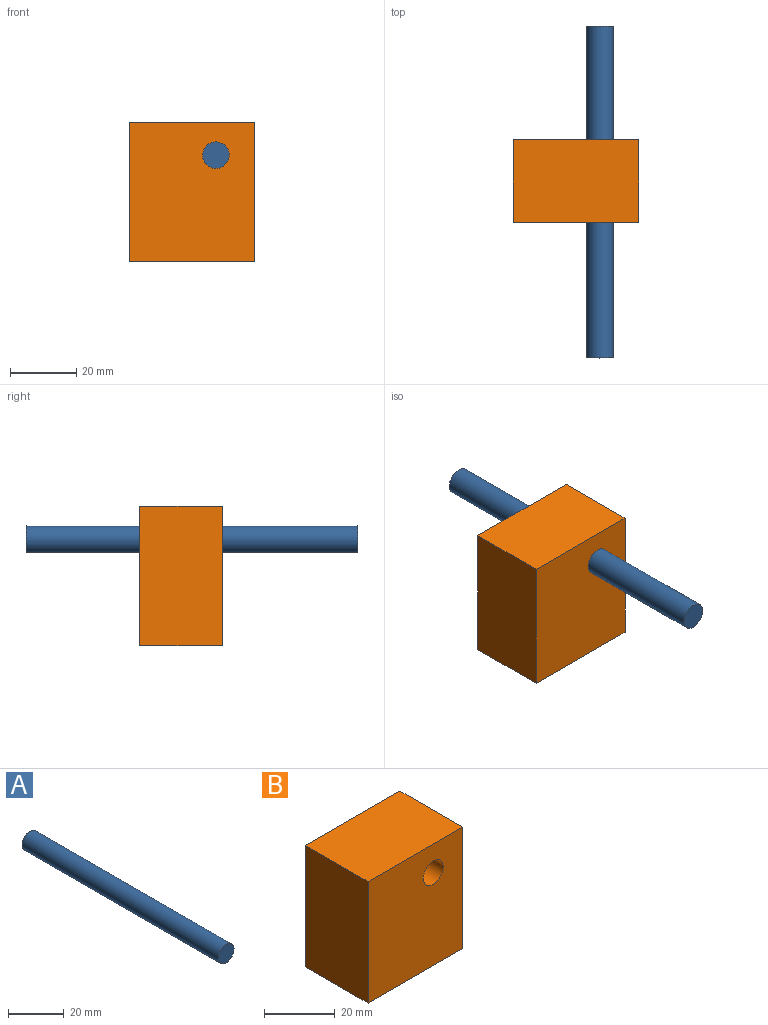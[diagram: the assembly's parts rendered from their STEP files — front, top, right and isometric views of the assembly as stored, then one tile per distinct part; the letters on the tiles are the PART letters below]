
ASSEMBLY  parts=2 mates=1
PART A: 3 faces, bbox 8x100x8 mm
  f0: cylinder r=4mm len=100mm, axis (0,1,0), area 2513.3mm2, adj f1,f2
  f1: plane 8x8mm, normal (0,-1,0), area 50.3mm2, adj f0
  f2: plane 8x8mm, normal (0,1,0), area 50.3mm2, adj f0
PART B: 7 faces, bbox 37.8x25x42.1 mm
  f0: plane 37.77x25mm, normal (0,0,1), area 944.2mm2, adj f1,f3,f4,f5
  f1: plane 42.05x25mm, normal (-1,0,0), area 1051.3mm2, adj f0,f2,f4,f5
  f2: plane 37.77x25mm, normal (0,0,-1), area 944.2mm2, adj f1,f3,f4,f5
  f3: plane 42.05x25mm, normal (1,0,0), area 1051.3mm2, adj f0,f2,f4,f5
  f4: plane 42.05x37.77mm, normal (0,-1,0), area 1538mm2, adj f0,f1,f2,f3,f6
  f5: plane 42.05x37.77mm, normal (0,1,0), area 1538mm2, adj f0,f1,f2,f3,f6
  f6: cylinder r=4mm len=25mm, axis (0,-1,0), area 628.3mm2, adj f4,f5
PLACE A t=(-2.34,34.2,-6.81)mm
PLACE B at identity
MATE slider A.f0 <-> B.f6  axis (0,1,0) through (8.08,34.2,10.71)mm
